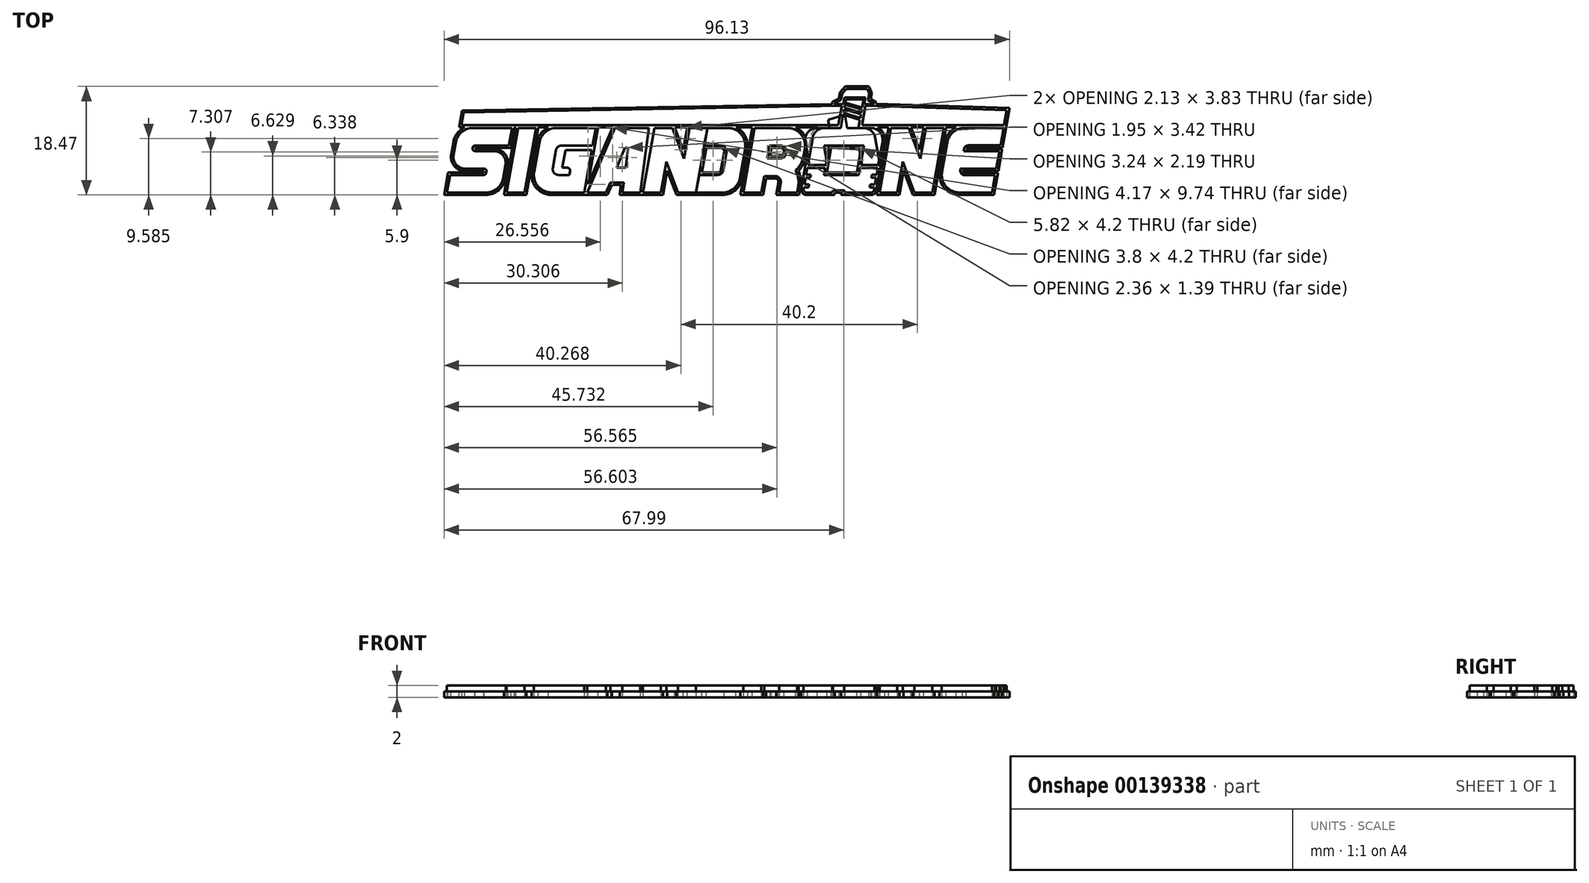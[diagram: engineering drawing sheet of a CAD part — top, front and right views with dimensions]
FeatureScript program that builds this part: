
annotation { "Feature Type Name" : "Feature", "Feature Type Description" : "" }
export const myFeature = defineFeature(function(context is Context, id is Id, definition is map)
    precondition{}
    {
        {
            var Q0;
            Q0=qCreatedBy(makeId("Top.planeOp"),FACE);
            var sketch = newSketch(context, id + "F0", { "sketchPlane" : qUnion([Q0])});
            skLineSegment(sketch, "E0", {"start": v(-0.12, -19.83) * mm, "end": v(-0.12, 13.35) * mm, "construction": true});
            skLineSegment(sketch, "E1.bottom", {"start": v(-3.34, 5.5) * mm, "end": v(-0.53, 5.5) * mm});
            skLineSegment(sketch, "E1.top", {"start": v(-6.37, -5.5) * mm, "end": v(-1.97, -5.5) * mm});
            skLineSegment(sketch, "E1.left", {"start": v(-5.31, 3.85) * mm, "end": v(-6.14, -0.83) * mm});
            skLineSegment(sketch, "E1.right", {"start": v(6.55, 3.15) * mm, "end": v(5.85, -0.83) * mm});
            skPoint(sketch, "E1.middle", {"position": v(0, 0) * mm});
            skLineSegment(sketch, "E2.0", {"start": v(-2.5, 2.5) * mm, "end": v(3.39, 2.5) * mm});
            skLineSegment(sketch, "E2.1", {"start": v(-2.5, 2.5) * mm, "end": v(-3.1, -0.83) * mm});
            skLineSegment(sketch, "E2.2", {"start": v(-3.39, -2.5) * mm, "end": v(2.5, -2.5) * mm});
            skLineSegment(sketch, "E2.3", {"start": v(3.39, 2.5) * mm, "end": v(2.8, -0.83) * mm});
            skLineSegment(sketch, "E3", {"start": v(-6.23, -1.33) * mm, "end": v(-3.18, -1.33) * mm});
            skLineSegment(sketch, "E4", {"start": v(-6.14, -0.83) * mm, "end": v(-3.1, -0.83) * mm});
            skLineSegment(sketch, "E5", {"start": v(-6.43, -2.5) * mm, "end": v(-5.64, -2.5) * mm});
            skLineSegment(sketch, "E6", {"start": v(-6.52, -2.98) * mm, "end": v(-5.73, -2.98) * mm});
            skLineSegment(sketch, "E7", {"start": v(-6.72, -4.14) * mm, "end": v(-5.93, -4.14) * mm});
            skLineSegment(sketch, "E8", {"start": v(-6.8, -4.64) * mm, "end": v(-6.02, -4.64) * mm});
            skLineSegment(sketch, "E9", {"start": v(-6.02, -4.64) * mm, "end": v(-5.93, -4.14) * mm});
            skLineSegment(sketch, "E10", {"start": v(4.38, -4.64) * mm, "end": v(4.47, -4.14) * mm});
            skLineSegment(sketch, "E11.trimOffspring", {"start": v(-6.8, -4.64) * mm, "end": v(-6.86, -4.91) * mm});
            skLineSegment(sketch, "E12.trimOffspring", {"start": v(-6.52, -2.98) * mm, "end": v(-6.72, -4.14) * mm});
            skLineSegment(sketch, "E13.trimOffspring", {"start": v(5.47, -2.98) * mm, "end": v(5.26, -4.14) * mm});
            skLineSegment(sketch, "E14.trimOffspring", {"start": v(5.17, -4.64) * mm, "end": v(5.1, -5.09) * mm});
            skLineSegment(sketch, "E15.trimOffspring", {"start": v(4.67, -2.98) * mm, "end": v(4.76, -2.5) * mm});
            skLineSegment(sketch, "E16.trimOffspring", {"start": v(4.67, -2.98) * mm, "end": v(5.47, -2.98) * mm});
            skLineSegment(sketch, "E17.trimOffspring", {"start": v(4.76, -2.5) * mm, "end": v(5.55, -2.5) * mm});
            skLineSegment(sketch, "E18.trimOffspring", {"start": v(4.47, -4.14) * mm, "end": v(5.26, -4.14) * mm});
            skLineSegment(sketch, "E19.trimOffspring", {"start": v(4.38, -4.64) * mm, "end": v(5.17, -4.64) * mm});
            skLineSegment(sketch, "E20.trimOffspring", {"start": v(-5.73, -2.98) * mm, "end": v(-5.64, -2.5) * mm});
            skLineSegment(sketch, "E21.trimOffspring", {"start": v(-6.23, -1.33) * mm, "end": v(-6.43, -2.5) * mm});
            skLineSegment(sketch, "E22.trimOffspring", {"start": v(5.76, -1.33) * mm, "end": v(5.55, -2.5) * mm});
            skLineSegment(sketch, "E23.trimOffspring", {"start": v(2.8, -0.83) * mm, "end": v(5.85, -0.83) * mm});
            skLineSegment(sketch, "E24.trimOffspring", {"start": v(2.71, -1.33) * mm, "end": v(5.76, -1.33) * mm});
            skLineSegment(sketch, "E25.trimOffspring", {"start": v(2.71, -1.33) * mm, "end": v(2.5, -2.5) * mm});
            skLineSegment(sketch, "E26.trimOffspring", {"start": v(-3.18, -1.33) * mm, "end": v(-3.39, -2.5) * mm});
            skLineSegment(sketch, "E27", {"start": v(0.97, 5.5) * mm, "end": v(1.83, 10.37) * mm, "construction": true});
            skLineSegment(sketch, "E28", {"start": v(-0.53, 5.5) * mm, "end": v(-0.13, 7.75) * mm});
            skLineSegment(sketch, "E29", {"start": v(0.33, 10.37) * mm, "end": v(3.33, 10.37) * mm});
            skLineSegment(sketch, "E30", {"start": v(3.33, 10.37) * mm, "end": v(3.08, 8.94) * mm});
            skLineSegment(sketch, "E31.trimOffspring", {"start": v(2.47, 5.5) * mm, "end": v(4.58, 5.5) * mm});
            skLineSegment(sketch, "E32", {"start": v(7.98, 5.5) * mm, "end": v(6.04, -5.5) * mm});
            skLineSegment(sketch, "E33", {"start": v(7.98, 5.5) * mm, "end": v(11.02, 5.5) * mm});
            skLineSegment(sketch, "E34", {"start": v(11.02, 5.5) * mm, "end": v(13, 0.27) * mm});
            skLineSegment(sketch, "E35", {"start": v(13, 0.27) * mm, "end": v(13.93, 5.5) * mm});
            skLineSegment(sketch, "E36", {"start": v(13.93, 5.5) * mm, "end": v(16.98, 5.5) * mm});
            skLineSegment(sketch, "E37", {"start": v(16.98, 5.5) * mm, "end": v(15.04, -5.5) * mm});
            skLineSegment(sketch, "E38", {"start": v(15.04, -5.5) * mm, "end": v(12, -5.5) * mm});
            skLineSegment(sketch, "E39", {"start": v(12, -5.5) * mm, "end": v(10, -0.27) * mm});
            skLineSegment(sketch, "E40", {"start": v(10, -0.27) * mm, "end": v(9.08, -5.5) * mm});
            skLineSegment(sketch, "E41", {"start": v(9.08, -5.5) * mm, "end": v(6.04, -5.5) * mm});
            skLineSegment(sketch, "E42", {"start": v(17.56, 3.02) * mm, "end": v(16.67, -1.98) * mm});
            skLineSegment(sketch, "E43", {"start": v(19.63, -5.5) * mm, "end": v(25.2, -5.5) * mm});
            skLineSegment(sketch, "E44", {"start": v(25.2, -5.5) * mm, "end": v(25.71, -2.55) * mm});
            skLineSegment(sketch, "E45", {"start": v(27.13, 5.5) * mm, "end": v(20.51, 5.5) * mm});
            skLineSegment(sketch, "E46", {"start": v(26.61, 2.55) * mm, "end": v(21.19, 2.55) * mm});
            skLineSegment(sketch, "E47", {"start": v(20.4, 1.88) * mm, "end": v(20.34, 1.5) * mm});
            skLineSegment(sketch, "E48", {"start": v(20.34, 1.5) * mm, "end": v(26.43, 1.5) * mm});
            skLineSegment(sketch, "E49", {"start": v(25.9, -1.45) * mm, "end": v(19.81, -1.45) * mm});
            skLineSegment(sketch, "E50", {"start": v(19.81, -1.45) * mm, "end": v(19.79, -1.6) * mm});
            skLineSegment(sketch, "E51", {"start": v(20.57, -2.55) * mm, "end": v(25.71, -2.55) * mm});
            skLineSegment(sketch, "E52.trimOffspring", {"start": v(25.9, -1.45) * mm, "end": v(26.43, 1.5) * mm});
            skLineSegment(sketch, "E53.trimOffspring", {"start": v(26.61, 2.55) * mm, "end": v(27.13, 5.5) * mm});
            skLineSegment(sketch, "E54", {"start": v(0.97, 5.5) * mm, "end": v(-0.9, -5.1) * mm, "construction": true});
            skLineSegment(sketch, "E55", {"start": v(-1.97, -5.5) * mm, "end": v(-1.9, -5.1) * mm});
            skLineSegment(sketch, "E56", {"start": v(-1.9, -5.1) * mm, "end": v(0.1, -5.1) * mm});
            skLineSegment(sketch, "E57", {"start": v(0.1, -5.1) * mm, "end": v(0.03, -5.5) * mm});
            skLineSegment(sketch, "E58.trimOffspring", {"start": v(0.03, -5.5) * mm, "end": v(4.6, -5.5) * mm});
            skPoint(sketch, "E59.visualSharp", {"position": v(-5.02, 5.5) * mm});
            skArc(sketch, "E59.filletArc", {"start": v(-3.34, 5.5) * mm, "mid": v(-4.63, 5.03) * mm, "end": v(-5.31, 3.85) * mm});
            skPoint(sketch, "E60.visualSharp", {"position": v(6.96, 5.5) * mm});
            skArc(sketch, "E60.filletArc", {"start": v(6.55, 3.15) * mm, "mid": v(6.11, 4.79) * mm, "end": v(4.58, 5.5) * mm});
            skPoint(sketch, "E61.visualSharp", {"position": v(-6.96, -5.5) * mm});
            skArc(sketch, "E61.filletArc", {"start": v(-6.86, -4.91) * mm, "mid": v(-6.75, -5.32) * mm, "end": v(-6.37, -5.5) * mm});
            skPoint(sketch, "E62.visualSharp", {"position": v(5.02, -5.5) * mm});
            skArc(sketch, "E62.filletArc", {"start": v(4.6, -5.5) * mm, "mid": v(4.92, -5.38) * mm, "end": v(5.1, -5.09) * mm});
            skPoint(sketch, "E63.visualSharp", {"position": v(18, 5.5) * mm});
            skArc(sketch, "E63.filletArc", {"start": v(20.51, 5.5) * mm, "mid": v(18.58, 4.8) * mm, "end": v(17.56, 3.02) * mm});
            skPoint(sketch, "E64.visualSharp", {"position": v(16.05, -5.5) * mm});
            skArc(sketch, "E64.filletArc", {"start": v(16.67, -1.98) * mm, "mid": v(17.33, -4.43) * mm, "end": v(19.63, -5.5) * mm});
            skPoint(sketch, "E65.visualSharp", {"position": v(20.52, 2.55) * mm});
            skArc(sketch, "E65.filletArc", {"start": v(21.19, 2.55) * mm, "mid": v(20.68, 2.36) * mm, "end": v(20.4, 1.88) * mm});
            skPoint(sketch, "E66.visualSharp", {"position": v(19.62, -2.55) * mm});
            skArc(sketch, "E66.filletArc", {"start": v(19.79, -1.6) * mm, "mid": v(19.96, -2.26) * mm, "end": v(20.57, -2.55) * mm});
            skLineSegment(sketch, "E67", {"start": v(-15.18, 5.5) * mm, "end": v(-17.12, -5.5) * mm});
            skLineSegment(sketch, "E68", {"start": v(-17.12, -5.5) * mm, "end": v(-14.07, -5.5) * mm});
            skLineSegment(sketch, "E69", {"start": v(-14.07, -5.5) * mm, "end": v(-13.57, -2.69) * mm});
            skLineSegment(sketch, "E70", {"start": v(-13.57, -2.69) * mm, "end": v(-11.72, -2.69) * mm});
            skLineSegment(sketch, "E71", {"start": v(-10.73, -3.86) * mm, "end": v(-11.02, -5.5) * mm});
            skLineSegment(sketch, "E72", {"start": v(-11.02, -5.5) * mm, "end": v(-7.98, -5.5) * mm});
            skLineSegment(sketch, "E73", {"start": v(-7.98, -5.5) * mm, "end": v(-7.78, -4.38) * mm});
            skLineSegment(sketch, "E74", {"start": v(-9.61, 5.5) * mm, "end": v(-15.18, 5.5) * mm});
            skLineSegment(sketch, "E75", {"start": v(-12.66, 2.5) * mm, "end": v(-13.04, 0.31) * mm});
            skLineSegment(sketch, "E76", {"start": v(-13.04, 0.31) * mm, "end": v(-10.84, 0.31) * mm});
            skLineSegment(sketch, "E77", {"start": v(-9.85, 1.14) * mm, "end": v(-9.82, 1.33) * mm});
            skLineSegment(sketch, "E78", {"start": v(-10.8, 2.5) * mm, "end": v(-12.66, 2.5) * mm});
            skPoint(sketch, "E79.visualSharp", {"position": v(-6.04, 5.5) * mm});
            skArc(sketch, "E79.filletArc", {"start": v(-6.66, 1.98) * mm, "mid": v(-7.32, 4.43) * mm, "end": v(-9.61, 5.5) * mm});
            skPoint(sketch, "E80.visualSharp", {"position": v(-10.53, -2.69) * mm});
            skArc(sketch, "E80.filletArc", {"start": v(-10.73, -3.86) * mm, "mid": v(-10.95, -3.04) * mm, "end": v(-11.72, -2.69) * mm});
            skPoint(sketch, "E81.visualSharp", {"position": v(-10, 0.31) * mm});
            skArc(sketch, "E81.filletArc", {"start": v(-10.84, 0.31) * mm, "mid": v(-10.2, 0.55) * mm, "end": v(-9.85, 1.14) * mm});
            skArc(sketch, "E82.filletArc", {"start": v(-9.82, 1.33) * mm, "mid": v(-10.04, 2.14) * mm, "end": v(-10.8, 2.5) * mm});
            skArc(sketch, "E83.0", {"start": v(-8.23, -1.72) * mm, "mid": v(-7.36, -0.67) * mm, "end": v(-6.9, 0.62) * mm});
            skArc(sketch, "E84.0", {"start": v(-7.78, -4.38) * mm, "mid": v(-7.78, -3.01) * mm, "end": v(-8.23, -1.72) * mm});
            skLineSegment(sketch, "E85.trimOffspring", {"start": v(-6.9, 0.62) * mm, "end": v(-6.66, 1.98) * mm});
            skLineSegment(sketch, "E86", {"start": v(-25.16, -5.5) * mm, "end": v(-20.65, -5.5) * mm});
            skLineSegment(sketch, "E87", {"start": v(-17.7, -3.02) * mm, "end": v(-16.81, 1.98) * mm});
            skLineSegment(sketch, "E88", {"start": v(-19.77, 5.5) * mm, "end": v(-23.22, 5.5) * mm});
            skLineSegment(sketch, "E89.0", {"start": v(-20.96, 2.5) * mm, "end": v(-23.75, 2.5) * mm});
            skLineSegment(sketch, "E89.1", {"start": v(-20.5, -1.67) * mm, "end": v(-19.97, 1.33) * mm});
            skLineSegment(sketch, "E89.2", {"start": v(-24.63, -2.5) * mm, "end": v(-21.49, -2.5) * mm});
            skPoint(sketch, "E90.visualSharp", {"position": v(-16.2, 5.5) * mm});
            skArc(sketch, "E90.filletArc", {"start": v(-16.81, 1.98) * mm, "mid": v(-17.47, 4.43) * mm, "end": v(-19.77, 5.5) * mm});
            skPoint(sketch, "E91.visualSharp", {"position": v(-18.13, -5.5) * mm});
            skArc(sketch, "E91.filletArc", {"start": v(-20.65, -5.5) * mm, "mid": v(-18.72, -4.8) * mm, "end": v(-17.7, -3.02) * mm});
            skArc(sketch, "E92.filletArc", {"start": v(-19.97, 1.33) * mm, "mid": v(-20.2, 2.14) * mm, "end": v(-20.96, 2.5) * mm});
            skArc(sketch, "E93.filletArc", {"start": v(-21.49, -2.5) * mm, "mid": v(-20.85, -2.27) * mm, "end": v(-20.5, -1.67) * mm});
            skLineSegment(sketch, "E94", {"start": v(-0.37, 9.28) * mm, "end": v(-64.66, 8.15) * mm});
            skLineSegment(sketch, "E95", {"start": v(-65.04, 6) * mm, "end": v(-0.95, 6) * mm});
            skLineSegment(sketch, "E96", {"start": v(-0.95, 6) * mm, "end": v(-0.37, 9.28) * mm});
            skLineSegment(sketch, "E97", {"start": v(3.64, 9.28) * mm, "end": v(3.07, 6) * mm});
            skLineSegment(sketch, "E98", {"start": v(3.07, 6) * mm, "end": v(27.22, 6) * mm});
            skLineSegment(sketch, "E99", {"start": v(27.67, 8.54) * mm, "end": v(3.64, 9.28) * mm});
            skLineSegment(sketch, "E100", {"start": v(27.22, 6) * mm, "end": v(27.67, 8.54) * mm});
            skLineSegment(sketch, "E101", {"start": v(-1.64, 9.55) * mm, "end": v(-1.63, 9.65) * mm});
            skLineSegment(sketch, "E102", {"start": v(-0.5, 10.25) * mm, "end": v(-0.3, 11.36) * mm});
            skLineSegment(sketch, "E103", {"start": v(0.4, 12.17) * mm, "end": v(-0.3, 11.36) * mm});
            skLineSegment(sketch, "E104", {"start": v(0.4, 12.17) * mm, "end": v(3.95, 12.17) * mm});
            skLineSegment(sketch, "E105", {"start": v(4.32, 11.36) * mm, "end": v(4.12, 10.25) * mm});
            skLineSegment(sketch, "E106", {"start": v(5.04, 9.65) * mm, "end": v(5.02, 9.53) * mm});
            skLineSegment(sketch, "E107", {"start": v(5.02, 9.53) * mm, "end": v(3.5, 9.58) * mm});
            skLineSegment(sketch, "E108", {"start": v(3.5, 9.58) * mm, "end": v(3.69, 10.67) * mm});
            skLineSegment(sketch, "E109", {"start": v(3.69, 10.67) * mm, "end": v(0.08, 10.67) * mm});
            skLineSegment(sketch, "E110", {"start": v(0.08, 10.67) * mm, "end": v(-0.12, 9.58) * mm});
            skLineSegment(sketch, "E111", {"start": v(-0.12, 9.58) * mm, "end": v(-1.64, 9.55) * mm});
            skLineSegment(sketch, "E112", {"start": v(-1.63, 9.65) * mm, "end": v(-0.5, 10.25) * mm});
            skLineSegment(sketch, "E113", {"start": v(5.04, 9.65) * mm, "end": v(4.12, 10.25) * mm});
            skPoint(sketch, "E114.orphan", {"position": v(4.37, 11.68) * mm});
            skPoint(sketch, "E115.orphan", {"position": v(-0.25, 11.68) * mm});
            skLineSegment(sketch, "E116", {"start": v(4.32, 11.36) * mm, "end": v(3.95, 12.17) * mm});
            skLineSegment(sketch, "E117", {"start": v(-23.75, 2.5) * mm, "end": v(-23.22, 5.5) * mm});
            skLineSegment(sketch, "E118", {"start": v(-24.63, -2.5) * mm, "end": v(-25.16, -5.5) * mm});
            skLineSegment(sketch, "E119", {"start": v(-64.66, 8.15) * mm, "end": v(-65.04, 6) * mm});
            skLineSegment(sketch, "E120", {"start": v(0.23, 9.8) * mm, "end": v(3.08, 8.94) * mm});
            skLineSegment(sketch, "E121", {"start": v(0.17, 9.5) * mm, "end": v(3.02, 8.64) * mm});
            skLineSegment(sketch, "E122", {"start": v(0.08, 8.95) * mm, "end": v(2.93, 8.1) * mm});
            skLineSegment(sketch, "E123", {"start": v(0.03, 8.66) * mm, "end": v(2.88, 7.8) * mm});
            skLineSegment(sketch, "E124", {"start": v(-0.08, 8.05) * mm, "end": v(2.77, 7.2) * mm});
            skLineSegment(sketch, "E125", {"start": v(-0.13, 7.75) * mm, "end": v(2.72, 6.9) * mm});
            skLineSegment(sketch, "E126", {"start": v(2.77, 7.2) * mm, "end": v(2.72, 6.9) * mm, "construction": true});
            skLineSegment(sketch, "E127", {"start": v(2.88, 7.8) * mm, "end": v(2.77, 7.2) * mm});
            skLineSegment(sketch, "E128", {"start": v(2.93, 8.1) * mm, "end": v(2.88, 7.8) * mm, "construction": true});
            skLineSegment(sketch, "E129", {"start": v(0.17, 9.5) * mm, "end": v(0.23, 9.8) * mm, "construction": true});
            skLineSegment(sketch, "E130", {"start": v(0.08, 8.95) * mm, "end": v(0.17, 9.5) * mm});
            skLineSegment(sketch, "E131", {"start": v(0.03, 8.66) * mm, "end": v(0.08, 8.95) * mm, "construction": true});
            skLineSegment(sketch, "E132", {"start": v(-0.08, 8.05) * mm, "end": v(0.03, 8.66) * mm});
            skLineSegment(sketch, "E133", {"start": v(-0.13, 7.75) * mm, "end": v(-0.08, 8.05) * mm, "construction": true});
            skLineSegment(sketch, "E134", {"start": v(0.23, 9.8) * mm, "end": v(0.33, 10.37) * mm});
            skLineSegment(sketch, "E135", {"start": v(3.08, 8.94) * mm, "end": v(3.02, 8.64) * mm, "construction": true});
            skLineSegment(sketch, "E136", {"start": v(3.02, 8.64) * mm, "end": v(2.93, 8.1) * mm});
            skLineSegment(sketch, "E137", {"start": v(2.72, 6.9) * mm, "end": v(2.47, 5.5) * mm});
            skSolve(sketch);
        }
        {
            var Q0;
            Q0=makeQuery(id+"F0.imprint","IMPRINT",FACE,{"disambiguationData":[TD([[makeQuery(id+"F0.imprint","IMPRINT",EDGE,{"derivedFrom":sQuery(id+"F0.wireOp",EDGE,"E1.bottom")}),-1.0]])]});
            var Q1;
            Q1=makeQuery(id+"F0.imprint","IMPRINT",FACE,{"disambiguationData":[TD([[makeQuery(id+"F0.imprint","IMPRINT",EDGE,{"derivedFrom":sQuery(id+"F0.wireOp",EDGE,"E1.top")}),1.0]])]});
            var Q2;
            Q2=makeQuery(id+"F0.imprint","IMPRINT",FACE,{"disambiguationData":[TD([[makeQuery(id+"F0.imprint","IMPRINT",EDGE,{"derivedFrom":sQuery(id+"F0.wireOp",EDGE,"E29")}),-1.0]])]});
            var Q3;
            Q3=makeQuery(id+"F0.imprint","IMPRINT",FACE,{"disambiguationData":[TD([[makeQuery(id+"F0.imprint","IMPRINT",EDGE,{"derivedFrom":sQuery(id+"F0.wireOp",EDGE,"E32")}),1.0]])]});
            var Q4;
            Q4=makeQuery(id+"F0.imprint","IMPRINT",FACE,{"disambiguationData":[TD([[makeQuery(id+"F0.imprint","IMPRINT",EDGE,{"derivedFrom":sQuery(id+"F0.wireOp",EDGE,"E42")}),1.0]])]});
            var Q5;
            Q5=makeQuery(id+"F0.imprint","IMPRINT",FACE,{"disambiguationData":[TD([[makeQuery(id+"F0.imprint","IMPRINT",EDGE,{"derivedFrom":sQuery(id+"F0.wireOp",EDGE,"E86")}),1.0]])]});
            var Q6;
            Q6=makeQuery(id+"F0.imprint","IMPRINT",FACE,{"disambiguationData":[TD([[makeQuery(id+"F0.imprint","IMPRINT",EDGE,{"derivedFrom":sQuery(id+"F0.wireOp",EDGE,"E94")}),1.0]])]});
            var Q7;
            Q7=makeQuery(id+"F0.imprint","IMPRINT",FACE,{"disambiguationData":[TD([[makeQuery(id+"F0.imprint","IMPRINT",EDGE,{"derivedFrom":sQuery(id+"F0.wireOp",EDGE,"E97")}),1.0]])]});
            var Q8;
            Q8=makeQuery(id+"F0.imprint","IMPRINT",FACE,{"disambiguationData":[TD([[makeQuery(id+"F0.imprint","IMPRINT",EDGE,{"derivedFrom":sQuery(id+"F0.wireOp",EDGE,"E101")}),-1.0]])]});
            var Q9;
            Q9=makeQuery(id+"F0.imprint","IMPRINT",FACE,{"disambiguationData":[TD([[makeQuery(id+"F0.imprint","IMPRINT",EDGE,{"derivedFrom":sQuery(id+"F0.wireOp",EDGE,"E121")}),-1.0]])]});
            var Q10;
            Q10=makeQuery(id+"F0.imprint","IMPRINT",FACE,{"disambiguationData":[TD([[makeQuery(id+"F0.imprint","IMPRINT",EDGE,{"derivedFrom":sQuery(id+"F0.wireOp",EDGE,"E123")}),-1.0]])]});
            var Q11;
            Q11=makeQuery(id+"F0.imprint","IMPRINT",FACE,{"disambiguationData":[TD([[makeQuery(id+"F0.imprint","IMPRINT",EDGE,{"derivedFrom":sQuery(id+"F0.wireOp",EDGE,"abPMcfiN-eTYI-O2cV-E9Ff-tLbUdmHkOaKU")}),1.0]])]});
            var Q12;
            Q12=makeQuery(id+"F0.imprint","IMPRINT",FACE,{"disambiguationData":[TD([[makeQuery(id+"F0.imprint","IMPRINT",EDGE,{"derivedFrom":sQuery(id+"F0.wireOp",EDGE,"E67")}),1.0]])]});
            extrude(context, id + "F1", {"entities" : qUnion([Q0, Q1, Q2, Q3, Q4, Q5, Q6, Q7, Q8, Q9, Q10, Q11, Q12]), "depth" : 2 * mm});
        }
        {
            var Q0;
            Q0=qCreatedBy(makeId("Top.planeOp"),FACE);
            var sketch = newSketch(context, id + "F2", { "sketchPlane" : qUnion([Q0])});
            skLineSegment(sketch, "E138", {"start": v(-56.44, 5.5) * mm, "end": v(-63.06, 5.5) * mm});
            skLineSegment(sketch, "E139", {"start": v(-56.44, 5.5) * mm, "end": v(-56.97, 2.5) * mm});
            skLineSegment(sketch, "E140", {"start": v(-56.97, 2.5) * mm, "end": v(-62.72, 2.5) * mm});
            skLineSegment(sketch, "E141", {"start": v(-63.12, 2.17) * mm, "end": v(-63.14, 2.04) * mm});
            skLineSegment(sketch, "E142", {"start": v(-62.75, 1.57) * mm, "end": v(-59.52, 1.57) * mm});
            skLineSegment(sketch, "E143", {"start": v(-57.55, -0.78) * mm, "end": v(-57.94, -3.02) * mm});
            skLineSegment(sketch, "E144", {"start": v(-60.9, -5.5) * mm, "end": v(-67.52, -5.5) * mm});
            skLineSegment(sketch, "E145", {"start": v(-67.52, -5.5) * mm, "end": v(-66.99, -2.5) * mm});
            skLineSegment(sketch, "E146", {"start": v(-66.99, -2.5) * mm, "end": v(-61.23, -2.5) * mm});
            skLineSegment(sketch, "E147", {"start": v(-60.84, -2.17) * mm, "end": v(-60.8, -1.9) * mm});
            skLineSegment(sketch, "E148", {"start": v(-61.18, -1.43) * mm, "end": v(-64.42, -1.43) * mm});
            skLineSegment(sketch, "E149", {"start": v(-66.39, 0.91) * mm, "end": v(-66.01, 3.02) * mm});
            skPoint(sketch, "E150.visualSharp", {"position": v(-65.58, 5.5) * mm});
            skArc(sketch, "E150.filletArc", {"start": v(-63.06, 5.5) * mm, "mid": v(-64.99, 4.8) * mm, "end": v(-66.01, 3.02) * mm});
            skPoint(sketch, "E151.visualSharp", {"position": v(-58.38, -5.5) * mm});
            skArc(sketch, "E151.filletArc", {"start": v(-60.9, -5.5) * mm, "mid": v(-58.97, -4.8) * mm, "end": v(-57.94, -3.02) * mm});
            skArc(sketch, "E152.filletArc", {"start": v(-62.72, 2.5) * mm, "mid": v(-62.98, 2.4) * mm, "end": v(-63.12, 2.17) * mm});
            skPoint(sketch, "E153.visualSharp", {"position": v(-63.22, 1.57) * mm});
            skArc(sketch, "E153.filletArc", {"start": v(-63.14, 2.04) * mm, "mid": v(-63.05, 1.7) * mm, "end": v(-62.75, 1.57) * mm});
            skPoint(sketch, "E154.visualSharp", {"position": v(-66.8, -1.43) * mm});
            skArc(sketch, "E154.filletArc", {"start": v(-66.39, 0.91) * mm, "mid": v(-65.95, -0.72) * mm, "end": v(-64.42, -1.43) * mm});
            skPoint(sketch, "E155.visualSharp", {"position": v(-57.13, 1.57) * mm});
            skArc(sketch, "E155.filletArc", {"start": v(-57.55, -0.78) * mm, "mid": v(-57.98, 0.85) * mm, "end": v(-59.52, 1.57) * mm});
            skPoint(sketch, "E156.visualSharp", {"position": v(-60.7, -1.43) * mm});
            skArc(sketch, "E156.filletArc", {"start": v(-60.8, -1.9) * mm, "mid": v(-60.88, -1.58) * mm, "end": v(-61.18, -1.43) * mm});
            skArc(sketch, "E157.filletArc", {"start": v(-61.23, -2.5) * mm, "mid": v(-60.97, -2.4) * mm, "end": v(-60.84, -2.17) * mm});
            skLineSegment(sketch, "E158", {"start": v(-55.42, 5.5) * mm, "end": v(-57.36, -5.5) * mm});
            skLineSegment(sketch, "E159", {"start": v(-57.36, -5.5) * mm, "end": v(-54.32, -5.5) * mm});
            skLineSegment(sketch, "E160", {"start": v(-54.32, -5.5) * mm, "end": v(-52.38, 5.5) * mm});
            skLineSegment(sketch, "E161", {"start": v(-52.38, 5.5) * mm, "end": v(-55.42, 5.5) * mm});
            skLineSegment(sketch, "E162", {"start": v(-42.22, 5.5) * mm, "end": v(-48.84, 5.5) * mm});
            skLineSegment(sketch, "E163", {"start": v(-51.8, 3.02) * mm, "end": v(-52.68, -1.98) * mm});
            skLineSegment(sketch, "E164", {"start": v(-49.73, -5.5) * mm, "end": v(-44.16, -5.5) * mm});
            skLineSegment(sketch, "E165", {"start": v(-44.16, -5.5) * mm, "end": v(-42.89, 1.72) * mm});
            skLineSegment(sketch, "E166", {"start": v(-42.89, 1.72) * mm, "end": v(-47.37, 1.72) * mm});
            skLineSegment(sketch, "E167", {"start": v(-47.37, 1.72) * mm, "end": v(-47.9, -1.28) * mm});
            skLineSegment(sketch, "E168", {"start": v(-47.9, -1.28) * mm, "end": v(-47.06, -1.28) * mm});
            skLineSegment(sketch, "E169", {"start": v(-46.57, -1.87) * mm, "end": v(-46.68, -2.5) * mm});
            skLineSegment(sketch, "E170", {"start": v(-46.68, -2.5) * mm, "end": v(-48.53, -2.5) * mm});
            skLineSegment(sketch, "E171", {"start": v(-49.52, -1.33) * mm, "end": v(-48.99, 1.67) * mm});
            skLineSegment(sketch, "E172", {"start": v(-48, 2.5) * mm, "end": v(-42.75, 2.5) * mm});
            skLineSegment(sketch, "E173", {"start": v(-42.75, 2.5) * mm, "end": v(-42.22, 5.5) * mm});
            skLineSegment(sketch, "E174", {"start": v(-43.66, -5.5) * mm, "end": v(-38.96, 5.5) * mm});
            skLineSegment(sketch, "E175", {"start": v(-38.96, 5.5) * mm, "end": v(-33.2, 5.5) * mm});
            skLineSegment(sketch, "E176", {"start": v(-33.2, 5.5) * mm, "end": v(-34.66, -5.5) * mm});
            skLineSegment(sketch, "E177", {"start": v(-34.66, -5.5) * mm, "end": v(-37.69, -5.5) * mm});
            skLineSegment(sketch, "E178", {"start": v(-37.69, -5.5) * mm, "end": v(-37.46, -3.77) * mm});
            skLineSegment(sketch, "E179", {"start": v(-37.46, -3.77) * mm, "end": v(-39.73, -3.77) * mm});
            skLineSegment(sketch, "E180", {"start": v(-39.73, -3.77) * mm, "end": v(-40.47, -5.5) * mm});
            skLineSegment(sketch, "E181", {"start": v(-40.47, -5.5) * mm, "end": v(-43.66, -5.5) * mm});
            skLineSegment(sketch, "E182", {"start": v(-37.27, 1.97) * mm, "end": v(-38.66, -1.27) * mm});
            skLineSegment(sketch, "E183", {"start": v(-38.66, -1.27) * mm, "end": v(-37.12, -1.27) * mm});
            skLineSegment(sketch, "E184", {"start": v(-37.12, -1.27) * mm, "end": v(-36.71, 1.81) * mm});
            skLineSegment(sketch, "E185", {"start": v(-32.22, 5.5) * mm, "end": v(-34.16, -5.5) * mm});
            skLineSegment(sketch, "E186", {"start": v(-32.22, 5.5) * mm, "end": v(-29.18, 5.5) * mm});
            skLineSegment(sketch, "E187", {"start": v(-29.18, 5.5) * mm, "end": v(-27.2, 0.27) * mm});
            skLineSegment(sketch, "E188", {"start": v(-27.2, 0.27) * mm, "end": v(-26.27, 5.5) * mm});
            skLineSegment(sketch, "E189", {"start": v(-26.27, 5.5) * mm, "end": v(-23.22, 5.5) * mm});
            skLineSegment(sketch, "E190", {"start": v(-23.22, 5.5) * mm, "end": v(-25.16, -5.5) * mm});
            skLineSegment(sketch, "E191", {"start": v(-25.16, -5.5) * mm, "end": v(-28.2, -5.5) * mm});
            skLineSegment(sketch, "E192", {"start": v(-28.2, -5.5) * mm, "end": v(-30.2, -0.27) * mm});
            skLineSegment(sketch, "E193", {"start": v(-30.2, -0.27) * mm, "end": v(-31.12, -5.5) * mm});
            skLineSegment(sketch, "E194", {"start": v(-31.12, -5.5) * mm, "end": v(-34.16, -5.5) * mm});
            skPoint(sketch, "E195.visualSharp", {"position": v(-51.36, 5.5) * mm});
            skArc(sketch, "E195.filletArc", {"start": v(-48.84, 5.5) * mm, "mid": v(-50.77, 4.8) * mm, "end": v(-51.8, 3.02) * mm});
            skPoint(sketch, "E196.visualSharp", {"position": v(-53.3, -5.5) * mm});
            skPoint(sketch, "E197.visualSharp", {"position": v(-36.43, 3.95) * mm});
            skArc(sketch, "E197.filletArc", {"start": v(-36.71, 1.81) * mm, "mid": v(-36.92, 2.14) * mm, "end": v(-37.27, 1.97) * mm});
            skPoint(sketch, "E198.visualSharp", {"position": v(-46.46, -1.28) * mm});
            skArc(sketch, "E198.filletArc", {"start": v(-46.57, -1.87) * mm, "mid": v(-46.68, -1.46) * mm, "end": v(-47.06, -1.28) * mm});
            skPoint(sketch, "E199.visualSharp", {"position": v(-46.68, -2.5) * mm});
            skPoint(sketch, "E200.visualSharp", {"position": v(-49.73, -2.5) * mm});
            skArc(sketch, "E200.filletArc", {"start": v(-49.52, -1.33) * mm, "mid": v(-49.3, -2.14) * mm, "end": v(-48.53, -2.5) * mm});
            skArc(sketch, "E201.filletArc", {"start": v(-48, 2.5) * mm, "mid": v(-48.65, 2.27) * mm, "end": v(-48.99, 1.67) * mm});
            skPoint(sketch, "E202.visualSharp", {"position": v(-44.16, -5.5) * mm});
            skArc(sketch, "E203.filletArc", {"start": v(-52.68, -1.98) * mm, "mid": v(-52.02, -4.43) * mm, "end": v(-49.73, -5.5) * mm});
            skSolve(sketch);
        }
        {
            var Q0;
            Q0=qSketchRegion(id+"F2",true);
            extrude(context, id + "F3", {"entities" : qUnion([Q0]), "depth" : 2 * mm});
        }
        {
            var Q0;
            Q0=makeQuery(id+"F3.opExtrude","CAP_FACE",FACE,{"disambiguationData":[OSD([sQuery(id+"F2.wireOp",EDGE,"E162"),sQuery(id+"F2.wireOp",EDGE,"E163"),sQuery(id+"F2.wireOp",EDGE,"E164"),sQuery(id+"F2.wireOp",EDGE,"E165"),sQuery(id+"F2.wireOp",EDGE,"E166"),sQuery(id+"F2.wireOp",EDGE,"E167"),sQuery(id+"F2.wireOp",EDGE,"E168"),sQuery(id+"F2.wireOp",EDGE,"E169"),sQuery(id+"F2.wireOp",EDGE,"E170"),sQuery(id+"F2.wireOp",EDGE,"E171"),sQuery(id+"F2.wireOp",EDGE,"E172"),sQuery(id+"F2.wireOp",EDGE,"E173"),sQuery(id+"F2.wireOp",EDGE,"E195.filletArc"),sQuery(id+"F2.wireOp",EDGE,"E198.filletArc"),sQuery(id+"F2.wireOp",EDGE,"E200.filletArc"),sQuery(id+"F2.wireOp",EDGE,"E201.filletArc"),sQuery(id+"F2.wireOp",EDGE,"E203.filletArc")])],"isStart":true});
            cPlane(context, id + "F4", {"entities" : qUnion([Q0]), "cplaneType" : CPlaneType.OFFSET, "offset" : 1 * mm, "oppositeDirection" : true, "width" : 150 * mm, "height" : 150 * mm});
        }
        {
            var Q0;
            Q0=qCreatedBy(id+"F4.planeOp",FACE);
            var sketch = newSketch(context, id + "F5", { "sketchPlane" : qUnion([Q0])});
            skLineSegment(sketch, "E204.0", {"start": v(-64.9, -8.45) * mm, "end": v(-65.42, -5.6) * mm});
            skLineSegment(sketch, "E204.1", {"start": v(-2.05, -9.55) * mm, "end": v(-64.9, -8.45) * mm});
            skArc(sketch, "E205.0", {"start": v(-60.9, 5.9) * mm, "mid": v(-58.71, 5.1) * mm, "end": v(-57.55, 3.1) * mm});
            skLineSegment(sketch, "E205.1", {"start": v(-61.18, 1.83) * mm, "end": v(-64.42, 1.83) * mm});
            skArc(sketch, "E205.2", {"start": v(-66.78, -0.98) * mm, "mid": v(-66.26, 0.98) * mm, "end": v(-64.42, 1.83) * mm});
            skLineSegment(sketch, "E205.3", {"start": v(-66.78, -0.98) * mm, "end": v(-66.4, -3.1) * mm});
            skArc(sketch, "E205.4", {"start": v(-64.46, -5.6) * mm, "mid": v(-65.74, -4.59) * mm, "end": v(-66.4, -3.1) * mm});
            skLineSegment(sketch, "E205.5", {"start": v(-61.18, 1.83) * mm, "end": v(-61.18, 1.83) * mm});
            skLineSegment(sketch, "E205.6", {"start": v(-61.23, 2.1) * mm, "end": v(-61.18, 1.83) * mm});
            skLineSegment(sketch, "E205.7", {"start": v(-61.23, 2.1) * mm, "end": v(-61.23, 2.1) * mm});
            skLineSegment(sketch, "E205.8", {"start": v(-67.32, 2.1) * mm, "end": v(-61.23, 2.1) * mm});
            skLineSegment(sketch, "E205.9", {"start": v(-68, 5.9) * mm, "end": v(-67.32, 2.1) * mm});
            skLineSegment(sketch, "E205.10", {"start": v(-60.9, 5.9) * mm, "end": v(-68, 5.9) * mm});
            skLineSegment(sketch, "E206.0", {"start": v(-54.33, 5.49) * mm, "end": v(-52.39, -5.5) * mm});
            skLineSegment(sketch, "E206.1", {"start": v(-57.35, 5.49) * mm, "end": v(-54.33, 5.49) * mm});
            skLineSegment(sketch, "E206.2", {"start": v(-55.41, -5.5) * mm, "end": v(-57.35, 5.49) * mm});
            skLineSegment(sketch, "E207.0", {"start": v(-54, 5.89) * mm, "end": v(-51.97, -5.6) * mm});
            skLineSegment(sketch, "E207.1", {"start": v(-57.83, 5.89) * mm, "end": v(-54, 5.89) * mm});
            skLineSegment(sketch, "E207.2", {"start": v(-55.8, -5.6) * mm, "end": v(-57.83, 5.89) * mm});
            skLineSegment(sketch, "E208.0", {"start": v(-57.15, 0.85) * mm, "end": v(-57.55, 3.1) * mm});
            skArc(sketch, "E208.1", {"start": v(-57.15, 0.85) * mm, "mid": v(-57.68, -1.1) * mm, "end": v(-59.52, -1.97) * mm});
            skLineSegment(sketch, "E208.2", {"start": v(-62.75, -1.97) * mm, "end": v(-59.52, -1.97) * mm});
            skLineSegment(sketch, "E208.3", {"start": v(-62.75, -1.97) * mm, "end": v(-62.75, -1.97) * mm});
            skLineSegment(sketch, "E208.4", {"start": v(-56.01, -5.6) * mm, "end": v(-56.63, -2.1) * mm});
            skLineSegment(sketch, "E208.5", {"start": v(-56.63, -2.1) * mm, "end": v(-62.72, -2.1) * mm});
            skLineSegment(sketch, "E208.6", {"start": v(-62.72, -2.1) * mm, "end": v(-62.72, -2.1) * mm});
            skLineSegment(sketch, "E208.7", {"start": v(-62.72, -2.1) * mm, "end": v(-62.75, -1.97) * mm});
            skLineSegment(sketch, "E209.0", {"start": v(-65.42, -5.6) * mm, "end": v(-64.46, -5.6) * mm});
            skLineSegment(sketch, "E210.0", {"start": v(-43.52, 4.14) * mm, "end": v(-41.8, -5.6) * mm});
            skArc(sketch, "E210.1", {"start": v(-50.24, -5.6) * mm, "mid": v(-51.53, -4.59) * mm, "end": v(-52.2, -3.1) * mm});
            skLineSegment(sketch, "E210.2", {"start": v(-52.2, -3.1) * mm, "end": v(-53.07, 1.9) * mm});
            skArc(sketch, "E210.3", {"start": v(-53.07, 1.9) * mm, "mid": v(-52.33, 4.69) * mm, "end": v(-49.73, 5.9) * mm});
            skLineSegment(sketch, "E210.4", {"start": v(-49.73, 5.9) * mm, "end": v(-43.83, 5.9) * mm});
            skLineSegment(sketch, "E211.trimOffspring", {"start": v(-18.37, -5.6) * mm, "end": v(-15.57, -5.6) * mm});
            skLineSegment(sketch, "E212.0", {"start": v(5.48, -9.84) * mm, "end": v(5.44, -9.62) * mm});
            skLineSegment(sketch, "E212.1", {"start": v(5.48, -9.84) * mm, "end": v(4.56, -10.44) * mm});
            skLineSegment(sketch, "E212.2", {"start": v(4.73, -11.42) * mm, "end": v(4.56, -10.44) * mm});
            skLineSegment(sketch, "E212.3", {"start": v(4.73, -11.42) * mm, "end": v(4.2, -12.57) * mm});
            skLineSegment(sketch, "E212.4", {"start": v(0.21, -12.57) * mm, "end": v(4.2, -12.57) * mm});
            skLineSegment(sketch, "E212.5", {"start": v(-2.05, -9.55) * mm, "end": v(-1.99, -9.91) * mm});
            skLineSegment(sketch, "E212.6", {"start": v(-1.99, -9.91) * mm, "end": v(-0.86, -10.51) * mm});
            skLineSegment(sketch, "E212.7", {"start": v(-0.86, -10.51) * mm, "end": v(-0.68, -11.54) * mm});
            skLineSegment(sketch, "E212.8", {"start": v(0.21, -12.57) * mm, "end": v(-0.68, -11.54) * mm});
            skLineSegment(sketch, "E213.0", {"start": v(28.14, -8.93) * mm, "end": v(5.44, -9.62) * mm});
            skLineSegment(sketch, "E213.1", {"start": v(27.61, -5.93) * mm, "end": v(28.14, -8.93) * mm});
            skLineSegment(sketch, "E214.0", {"start": v(26.95, -2.15) * mm, "end": v(27.53, -5.43) * mm});
            skLineSegment(sketch, "E214.1", {"start": v(26.95, -2.15) * mm, "end": v(21.19, -2.15) * mm});
            skArc(sketch, "E214.2", {"start": v(21.19, -2.15) * mm, "mid": v(20.97, -2.08) * mm, "end": v(20.82, -1.9) * mm});
            skLineSegment(sketch, "E214.3", {"start": v(20.82, -1.9) * mm, "end": v(26.9, -1.9) * mm});
            skLineSegment(sketch, "E214.4", {"start": v(26.24, 1.85) * mm, "end": v(26.9, -1.9) * mm});
            skLineSegment(sketch, "E214.5", {"start": v(25.53, 5.9) * mm, "end": v(26.19, 2.15) * mm});
            skLineSegment(sketch, "E214.6", {"start": v(20.57, 2.15) * mm, "end": v(26.19, 2.15) * mm});
            skArc(sketch, "E214.7", {"start": v(20.19, 1.85) * mm, "mid": v(20.33, 2.06) * mm, "end": v(20.57, 2.15) * mm});
            skLineSegment(sketch, "E214.8", {"start": v(26.24, 1.85) * mm, "end": v(20.19, 1.85) * mm});
            skLineSegment(sketch, "E215", {"start": v(27.53, -5.43) * mm, "end": v(27.61, -5.93) * mm});
            skLineSegment(sketch, "E216.0", {"start": v(19.63, 5.9) * mm, "end": v(25.53, 5.9) * mm});
            skArc(sketch, "E216.1", {"start": v(16.28, 1.9) * mm, "mid": v(17.02, 4.69) * mm, "end": v(19.63, 5.9) * mm});
            skLineSegment(sketch, "E216.2", {"start": v(17.16, -3.1) * mm, "end": v(16.28, 1.9) * mm});
            skArc(sketch, "E216.3", {"start": v(19.11, -5.6) * mm, "mid": v(17.83, -4.59) * mm, "end": v(17.16, -3.1) * mm});
            skLineSegment(sketch, "E217.0", {"start": v(7.59, -5.6) * mm, "end": v(5.56, 5.9) * mm});
            skLineSegment(sketch, "E217.1", {"start": v(9.42, 5.9) * mm, "end": v(5.56, 5.9) * mm});
            skLineSegment(sketch, "E217.2", {"start": v(17.4, -5.6) * mm, "end": v(15.37, 5.9) * mm});
            skLineSegment(sketch, "E217.3", {"start": v(15.37, 5.9) * mm, "end": v(11.72, 5.9) * mm});
            skLineSegment(sketch, "E217.4", {"start": v(11.72, 5.9) * mm, "end": v(10.15, 1.77) * mm});
            skLineSegment(sketch, "E217.5", {"start": v(10.15, 1.77) * mm, "end": v(9.42, 5.9) * mm});
            skLineSegment(sketch, "E218.0", {"start": v(12.87, -1.77) * mm, "end": v(13.54, -5.6) * mm});
            skLineSegment(sketch, "E218.1", {"start": v(11.41, -5.6) * mm, "end": v(12.87, -1.77) * mm});
            skLineSegment(sketch, "E219.trimOffspring", {"start": v(17.4, -5.6) * mm, "end": v(19.11, -5.6) * mm});
            skLineSegment(sketch, "E220.0", {"start": v(-43.52, 4.14) * mm, "end": v(-39.35, -5.6) * mm});
            skLineSegment(sketch, "E220.1", {"start": v(-40.2, 5.9) * mm, "end": v(-44.27, 5.9) * mm});
            skLineSegment(sketch, "E220.2", {"start": v(-34.66, 5.9) * mm, "end": v(-38.15, 5.9) * mm});
            skLineSegment(sketch, "E220.3", {"start": v(-38.15, 5.9) * mm, "end": v(-37.91, 4.17) * mm});
            skLineSegment(sketch, "E220.4", {"start": v(-37.91, 4.17) * mm, "end": v(-39.46, 4.17) * mm});
            skLineSegment(sketch, "E220.5", {"start": v(-39.46, 4.17) * mm, "end": v(-40.2, 5.9) * mm});
            skLineSegment(sketch, "E221.0", {"start": v(-30.78, 5.9) * mm, "end": v(-34.16, 5.9) * mm});
            skLineSegment(sketch, "E221.1", {"start": v(-30.05, 1.77) * mm, "end": v(-30.78, 5.9) * mm});
            skLineSegment(sketch, "E221.2", {"start": v(-28.48, 5.9) * mm, "end": v(-30.05, 1.77) * mm});
            skLineSegment(sketch, "E221.3", {"start": v(-25.16, 5.9) * mm, "end": v(-28.48, 5.9) * mm});
            skArc(sketch, "E221.4", {"start": v(-16.42, -1.9) * mm, "mid": v(-16.76, -4.09) * mm, "end": v(-18.37, -5.6) * mm});
            skLineSegment(sketch, "E221.5", {"start": v(-17.3, 3.1) * mm, "end": v(-16.42, -1.9) * mm});
            skArc(sketch, "E221.6", {"start": v(-20.65, 5.9) * mm, "mid": v(-18.46, 5.1) * mm, "end": v(-17.3, 3.1) * mm});
            skLineSegment(sketch, "E221.7", {"start": v(-25.16, 5.9) * mm, "end": v(-20.65, 5.9) * mm});
            skArc(sketch, "E222.0", {"start": v(-6.26, -1.9) * mm, "mid": v(-6.6, -4.09) * mm, "end": v(-8.22, -5.6) * mm});
            skLineSegment(sketch, "E222.1", {"start": v(-6.5, -0.55) * mm, "end": v(-6.26, -1.9) * mm});
            skLineSegment(sketch, "E222.2", {"start": v(-13.24, 3.09) * mm, "end": v(-11.72, 3.09) * mm});
            skLineSegment(sketch, "E222.3", {"start": v(-13.73, 5.9) * mm, "end": v(-13.24, 3.09) * mm});
            skLineSegment(sketch, "E222.4", {"start": v(-17.6, 5.9) * mm, "end": v(-13.73, 5.9) * mm});
            skLineSegment(sketch, "E222.5", {"start": v(-15.57, -5.6) * mm, "end": v(-17.6, 5.9) * mm});
            skArc(sketch, "E222.6", {"start": v(-11.13, 3.8) * mm, "mid": v(-11.26, 3.3) * mm, "end": v(-11.72, 3.09) * mm});
            skLineSegment(sketch, "E222.7", {"start": v(-11.13, 3.8) * mm, "end": v(-11.5, 5.9) * mm});
            skLineSegment(sketch, "E222.8", {"start": v(-11.5, 5.9) * mm, "end": v(-7.64, 5.9) * mm});
            skLineSegment(sketch, "E222.9", {"start": v(-7.64, 5.9) * mm, "end": v(-7.39, 4.45) * mm});
            skArc(sketch, "E222.10", {"start": v(-7.39, 4.45) * mm, "mid": v(-7.36, 3.1) * mm, "end": v(-7.74, 1.8) * mm});
            skArc(sketch, "E222.11", {"start": v(-7.74, 1.8) * mm, "mid": v(-6.94, 0.73) * mm, "end": v(-6.5, -0.55) * mm});
            skLineSegment(sketch, "E223.0", {"start": v(-5.7, -3.92) * mm, "end": v(-7.25, 4.84) * mm});
            skArc(sketch, "E223.1", {"start": v(-4.5, -5.6) * mm, "mid": v(-5.3, -4.9) * mm, "end": v(-5.7, -3.92) * mm});
            skArc(sketch, "E224.0", {"start": v(4.6, 5.9) * mm, "mid": v(5.18, 5.69) * mm, "end": v(5.49, 5.16) * mm});
            skLineSegment(sketch, "E224.1", {"start": v(-0.45, 5.9) * mm, "end": v(4.6, 5.9) * mm});
            skLineSegment(sketch, "E224.2", {"start": v(-0.38, 5.5) * mm, "end": v(-0.45, 5.9) * mm});
            skArc(sketch, "E224.3", {"start": v(-7.25, 4.84) * mm, "mid": v(-7.06, 5.58) * mm, "end": v(-6.37, 5.9) * mm});
            skLineSegment(sketch, "E224.4", {"start": v(-6.37, 5.9) * mm, "end": v(-1.63, 5.9) * mm});
            skLineSegment(sketch, "E224.5", {"start": v(-1.63, 5.9) * mm, "end": v(-1.56, 5.5) * mm});
            skLineSegment(sketch, "E224.6", {"start": v(-1.56, 5.5) * mm, "end": v(-0.38, 5.5) * mm});
            skArc(sketch, "E225.0", {"start": v(6.94, -3.08) * mm, "mid": v(6.74, -4.53) * mm, "end": v(5.74, -5.6) * mm});
            skLineSegment(sketch, "E225.1", {"start": v(6.94, -3.08) * mm, "end": v(5.49, 5.16) * mm});
            skLineSegment(sketch, "E226.trimOffspring", {"start": v(-8.22, -5.6) * mm, "end": v(-4.5, -5.6) * mm});
            skLineSegment(sketch, "E227", {"start": v(-34.66, 5.9) * mm, "end": v(-34.16, 5.9) * mm});
            skLineSegment(sketch, "E228", {"start": v(-41.8, -5.6) * mm, "end": v(-39.35, -5.6) * mm});
            skLineSegment(sketch, "E229.0", {"start": v(-27.33, -1.77) * mm, "end": v(-26.66, -5.6) * mm});
            skLineSegment(sketch, "E229.1", {"start": v(-28.79, -5.6) * mm, "end": v(-27.33, -1.77) * mm});
            skLineSegment(sketch, "E230", {"start": v(-56.01, -5.6) * mm, "end": v(-55.8, -5.6) * mm});
            skLineSegment(sketch, "E231.trimOffspring", {"start": v(-51.97, -5.6) * mm, "end": v(-50.24, -5.6) * mm});
            skLineSegment(sketch, "E232.trimOffspring", {"start": v(-28.79, -5.6) * mm, "end": v(-26.66, -5.6) * mm});
            skLineSegment(sketch, "E233", {"start": v(5.74, -5.6) * mm, "end": v(7.59, -5.6) * mm});
            skLineSegment(sketch, "E234", {"start": v(11.41, -5.6) * mm, "end": v(13.54, -5.6) * mm});
            skLineSegment(sketch, "E235.1", {"start": v(-2.17, -2.1) * mm, "end": v(2.91, -2.1) * mm});
            skLineSegment(sketch, "E235.2", {"start": v(2.91, -2.1) * mm, "end": v(2.17, 2.1) * mm});
            skLineSegment(sketch, "E236.1", {"start": v(-2.91, 2.1) * mm, "end": v(2.17, 2.1) * mm});
            skLineSegment(sketch, "E237", {"start": v(-2.17, -2.1) * mm, "end": v(-2.91, 2.1) * mm});
            skLineSegment(sketch, "E238.0", {"start": v(-20.96, -2.1) * mm, "end": v(-23.42, -2.1) * mm});
            skLineSegment(sketch, "E238.1", {"start": v(-24.16, 2.1) * mm, "end": v(-21.49, 2.1) * mm});
            skArc(sketch, "E238.2", {"start": v(-21.49, 2.1) * mm, "mid": v(-21.1, 1.96) * mm, "end": v(-20.9, 1.6) * mm});
            skLineSegment(sketch, "E238.3", {"start": v(-20.9, 1.6) * mm, "end": v(-20.37, -1.4) * mm});
            skArc(sketch, "E238.4", {"start": v(-20.37, -1.4) * mm, "mid": v(-20.5, -1.89) * mm, "end": v(-20.96, -2.1) * mm});
            skLineSegment(sketch, "E239.0", {"start": v(-23.42, -2.1) * mm, "end": v(-24.16, 2.1) * mm});
            skLineSegment(sketch, "E240.0", {"start": v(-10.8, -2.1) * mm, "end": v(-12.32, -2.1) * mm});
            skLineSegment(sketch, "E240.1", {"start": v(-12.57, -0.71) * mm, "end": v(-10.84, -0.71) * mm});
            skArc(sketch, "E240.2", {"start": v(-10.84, -0.71) * mm, "mid": v(-10.45, -0.85) * mm, "end": v(-10.25, -1.2) * mm});
            skLineSegment(sketch, "E240.3", {"start": v(-12.32, -2.1) * mm, "end": v(-12.57, -0.71) * mm});
            skLineSegment(sketch, "E240.4", {"start": v(-10.25, -1.2) * mm, "end": v(-10.21, -1.4) * mm});
            skArc(sketch, "E240.5", {"start": v(-10.21, -1.4) * mm, "mid": v(-10.35, -1.89) * mm, "end": v(-10.8, -2.1) * mm});
            skSolve(sketch);
        }
        {
            var Q0;
            Q0=qSketchRegion(id+"F5",true);
            extrude(context, id + "F6", {"entities" : qUnion([Q0]), "depth" : 1 * mm});
        }
        {
            var Q0;
            Q0=makeQuery(id+"F1.opExtrude","SWEPT_BODY",BODY,{"disambiguationData":[OSD([sQuery(id+"F0.wireOp",EDGE,"E1.bottom"),sQuery(id+"F0.wireOp",EDGE,"E1.left"),sQuery(id+"F0.wireOp",EDGE,"E1.right"),sQuery(id+"F0.wireOp",EDGE,"E2.0"),sQuery(id+"F0.wireOp",EDGE,"E2.1"),sQuery(id+"F0.wireOp",EDGE,"E2.3"),sQuery(id+"F0.wireOp",EDGE,"E4"),sQuery(id+"F0.wireOp",EDGE,"E23.trimOffspring"),sQuery(id+"F0.wireOp",EDGE,"E28"),sQuery(id+"F0.wireOp",EDGE,"E31.trimOffspring"),sQuery(id+"F0.wireOp",EDGE,"E59.filletArc"),sQuery(id+"F0.wireOp",EDGE,"E60.filletArc"),sQuery(id+"F0.wireOp",EDGE,"E125"),sQuery(id+"F0.wireOp",EDGE,"E137")])]});
            var Q1;
            Q1=qCreatedBy(makeId("Right.planeOp"),FACE);
            mirror(context, id + "F7", {"entities" : qUnion([Q0]), "mirrorPlane" : qUnion([Q1])});
        }
    });
